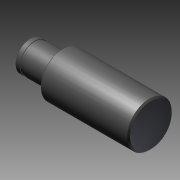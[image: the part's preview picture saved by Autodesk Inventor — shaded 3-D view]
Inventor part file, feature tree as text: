
AUTODESK INVENTOR PART (.ipt)
format: ipt  version: 2016 (Build 200138000, 138)  size: 139,264 bytes
history: native  units: mm
features: revolve x2, sketch x2
ambient origin geometry x8: Origin, YZ Plane, XZ Plane, XY Plane, X Axis, Y Axis, Z Axis, Center Point
bodies: Solid1 (feature_tree)
feature tree (4):
  revolve  "Revolution1"  Angle=360.0deg
  revolve  "Revolution2"  [1 undecoded]
  sketch  "Sketch_1"  dims[d0=360.0deg d1=360.0deg]
  sketch  "Sketch_40"
note: 1 required parameter value undecoded (feature->parameter linkage not recoverable at this tier; creation-order binding heuristic only, values carry confidence <= 0.55)
